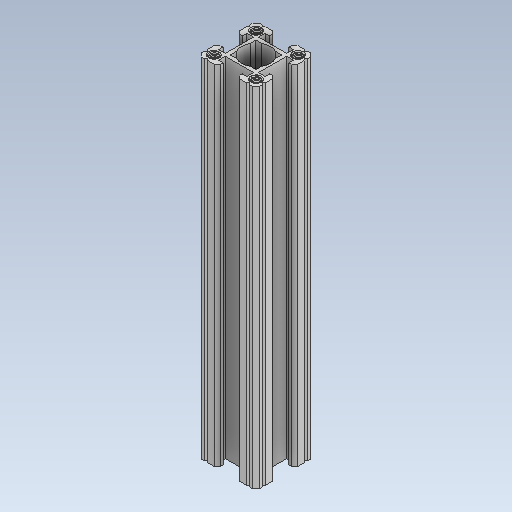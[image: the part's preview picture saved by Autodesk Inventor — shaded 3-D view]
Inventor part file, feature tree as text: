
AUTODESK INVENTOR PART (.ipt)
format: ipt  version: 2020 (Build 240168000, 168)  size: 2,937,856 bytes
history: native  units: in
note: dims shown in document units (in); Inventor stores cm internally (conversion verified against a paired STEP export)
features: mirror x1
ambient origin geometry x8: Origin, YZ Plane, XZ Plane, XY Plane, X Axis, Y Axis, Z Axis, Center Point
bodies: Solid1 (feature_tree)
feature tree (1):
  mirror  "Mirror1"
